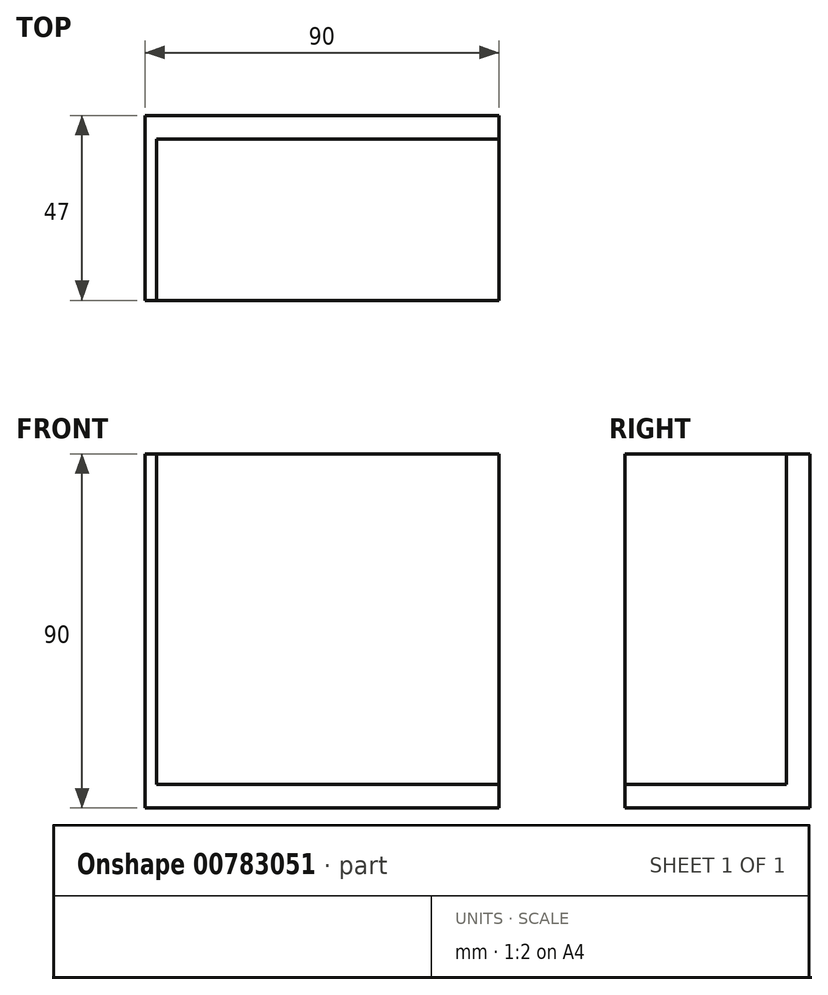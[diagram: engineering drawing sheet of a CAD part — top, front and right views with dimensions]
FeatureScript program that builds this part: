
annotation { "Feature Type Name" : "Feature", "Feature Type Description" : "" }
export const myFeature = defineFeature(function(context is Context, id is Id, definition is map)
    precondition{}
    {
        {
            var Q0;
            Q0=qCreatedBy(makeId("Right.planeOp"),FACE);
            var sketch = newSketch(context, id + "F0", { "sketchPlane" : qUnion([Q0])});
            skLineSegment(sketch, "E0", {"start": v(47, 90) * mm, "end": v(47, 0) * mm});
            skLineSegment(sketch, "E1", {"start": v(47, 0) * mm, "end": v(0, 0) * mm});
            skLineSegment(sketch, "E2", {"start": v(0, 0) * mm, "end": v(0, 6) * mm});
            skLineSegment(sketch, "E3", {"start": v(0, 6) * mm, "end": v(41, 6) * mm});
            skLineSegment(sketch, "E4", {"start": v(47, 90) * mm, "end": v(41, 90) * mm});
            skLineSegment(sketch, "E5", {"start": v(41, 90) * mm, "end": v(41, 6) * mm});
            skSolve(sketch);
        }
        {
            var Q0;
            Q0=makeQuery(id+"F0.imprint","IMPRINT",FACE,{"disambiguationData":[TD([[makeQuery(id+"F0.imprint","IMPRINT",EDGE,{"derivedFrom":sQuery(id+"F0.wireOp",EDGE,"E0")}),-1.0]])]});
            extrude(context, id + "F1", {"entities" : qUnion([Q0]), "depth" : 90 * mm, "offsetDistance" : 25 * mm});
        }
        {
            var Q0;
            Q0=makeQuery(id+"F1.opExtrude","CAP_FACE",FACE,{"disambiguationData":[OSD([sQuery(id+"F0.wireOp",EDGE,"E0"),sQuery(id+"F0.wireOp",EDGE,"E1"),sQuery(id+"F0.wireOp",EDGE,"E2"),sQuery(id+"F0.wireOp",EDGE,"E3"),sQuery(id+"F0.wireOp",EDGE,"E4"),sQuery(id+"F0.wireOp",EDGE,"E5")])],"isStart":false});
            var sketch = newSketch(context, id + "F2", { "sketchPlane" : qUnion([Q0])});
            skLineSegment(sketch, "E6.bottom", {"start": v(47, 0) * mm, "end": v(0, 0) * mm});
            skLineSegment(sketch, "E6.top", {"start": v(47, 90) * mm, "end": v(0, 90) * mm});
            skLineSegment(sketch, "E6.left", {"start": v(47, 0) * mm, "end": v(47, 90) * mm});
            skLineSegment(sketch, "E6.right", {"start": v(0, 0) * mm, "end": v(0, 90) * mm});
            skSolve(sketch);
        }
        {
            var Q0;
            Q0=makeQuery(id+"F1.opExtrude","CAP_FACE",FACE,{"disambiguationData":[OSD([sQuery(id+"F0.wireOp",EDGE,"E0"),sQuery(id+"F0.wireOp",EDGE,"E1"),sQuery(id+"F0.wireOp",EDGE,"E2"),sQuery(id+"F0.wireOp",EDGE,"E3"),sQuery(id+"F0.wireOp",EDGE,"E4"),sQuery(id+"F0.wireOp",EDGE,"E5")])],"isStart":true});
            var sketch = newSketch(context, id + "F3", { "sketchPlane" : qUnion([Q0])});
            skLineSegment(sketch, "E7.bottom", {"start": v(-47, 0) * mm, "end": v(0, 0) * mm});
            skLineSegment(sketch, "E7.top", {"start": v(-47, 90) * mm, "end": v(0, 90) * mm});
            skLineSegment(sketch, "E7.left", {"start": v(-47, 0) * mm, "end": v(-47, 90) * mm});
            skLineSegment(sketch, "E7.right", {"start": v(0, 0) * mm, "end": v(0, 90) * mm});
            skSolve(sketch);
        }
        {
            var Q0;
            Q0 = qSketchRegion(id + "F3", true);
            extrude(context, id + "F4", {"entities" : qUnion([Q0]), "operationType" : NewBodyOperationType.ADD, "oppositeDirection" : true, "depth" : 3 * mm, "offsetDistance" : 25 * mm});
        }
        {
            var Q0;
            Q0=makeQuery(id+"F4.boolean.opBoolean","MERGE",FACE,{"derivedFrom":[makeQuery(id+"FkpLQv1gJzUen6x_1.boolean.opBoolean","MERGE",FACE,{"derivedFrom":[makeQuery(id+"F1.opExtrude","SWEPT_FACE",FACE,{"disambiguationData":[OSD([sQuery(id+"F0.wireOp",EDGE,"E2")])]}),makeQuery(id+"FkpLQv1gJzUen6x_1.opExtrude","SWEPT_FACE",FACE,{"disambiguationData":[OSD([sQuery(id+"F2.wireOp",EDGE,"E6.right")])]})]}),makeQuery(id+"F4.opExtrude","SWEPT_FACE",FACE,{"disambiguationData":[OSD([sQuery(id+"F3.wireOp",EDGE,"E7.right")])]})]});
            var sketch = newSketch(context, id + "F5", { "sketchPlane" : qUnion([Q0])});
            skLineSegment(sketch, "E8", {"start": v(90, 3) * mm, "end": v(75, 3) * mm});
            skLineSegment(sketch, "E9", {"start": v(75, 3) * mm, "end": v(55, 3) * mm});
            skLineSegment(sketch, "E10", {"start": v(55, 3) * mm, "end": v(35, 3) * mm});
            skLineSegment(sketch, "E11", {"start": v(35, 3) * mm, "end": v(15, 3) * mm});
            skLineSegment(sketch, "E12", {"start": v(15, 3) * mm, "end": v(0, 3) * mm});
            skCircle(sketch, "E13", {"center": v(75, 3) * mm, "radius": 1.5 * mm});
            skCircle(sketch, "E14", {"center": v(55, 3) * mm, "radius": 1.5 * mm});
            skCircle(sketch, "E15", {"center": v(35, 3) * mm, "radius": 1.5 * mm});
            skCircle(sketch, "E16", {"center": v(15, 3) * mm, "radius": 1.5 * mm});
            skSolve(sketch);
        }
        {
            var Q0;
            Q0=sQuery(id+"F5.wireOp",EDGE,"E13");
            var Q1;
            Q1=sQuery(id+"F5.wireOp",EDGE,"E14");
            var Q2;
            Q2=sQuery(id+"F5.wireOp",EDGE,"E15");
            var Q3;
            Q3=sQuery(id+"F5.wireOp",EDGE,"E16");
            extrude(context, id + "F6", {"bodyType" : ToolBodyType.SURFACE, "surfaceEntities" : qUnion([Q0, Q1, Q2, Q3]), "depth" : 8 * mm, "offsetDistance" : 25 * mm});
        }
    });
